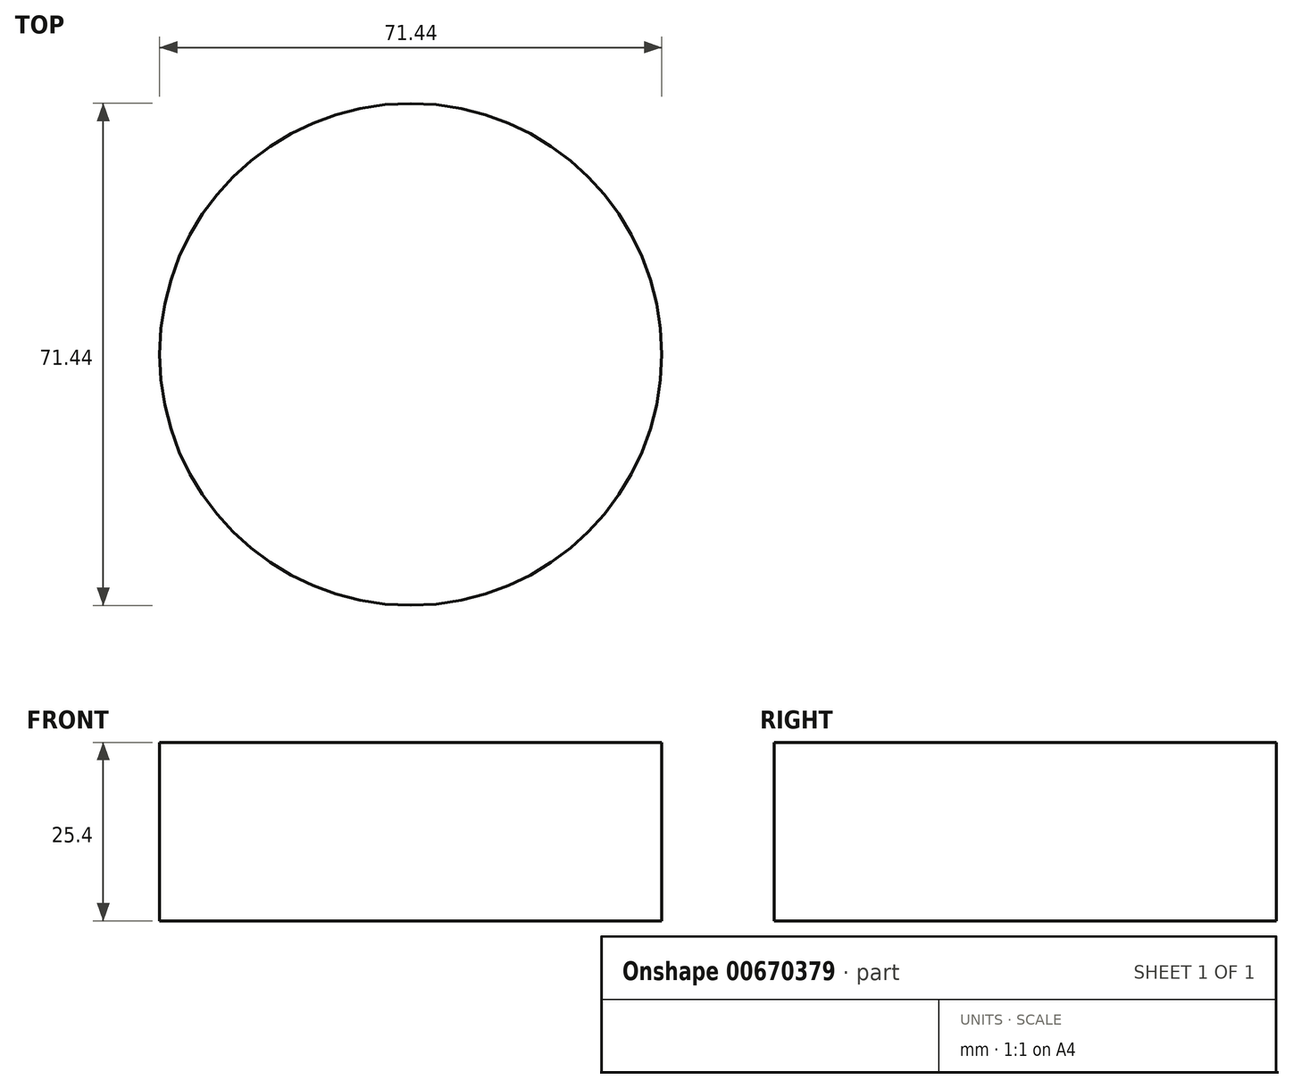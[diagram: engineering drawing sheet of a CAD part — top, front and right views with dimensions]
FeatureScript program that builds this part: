
annotation { "Feature Type Name" : "Feature", "Feature Type Description" : "" }
export const myFeature = defineFeature(function(context is Context, id is Id, definition is map)
    precondition{}
    {
        {
            var Q0;
            Q0=qCreatedBy(makeId("Top.planeOp"),FACE);
            var sketch = newSketch(context, id + "F0", { "sketchPlane" : qUnion([Q0])});
            skCircle(sketch, "E0", {"center": v(0, -32.47) * mm, "radius": 35.72 * mm});
            skSolve(sketch);
        }
        {
            var Q0;
            Q0 = qSketchRegion(id + "F0", true);
            extrude(context, id + "F1", {"entities" : qUnion([Q0]), "depth" : 25.4 * mm, "offsetDistance" : 25.4 * mm});
        }
    });
